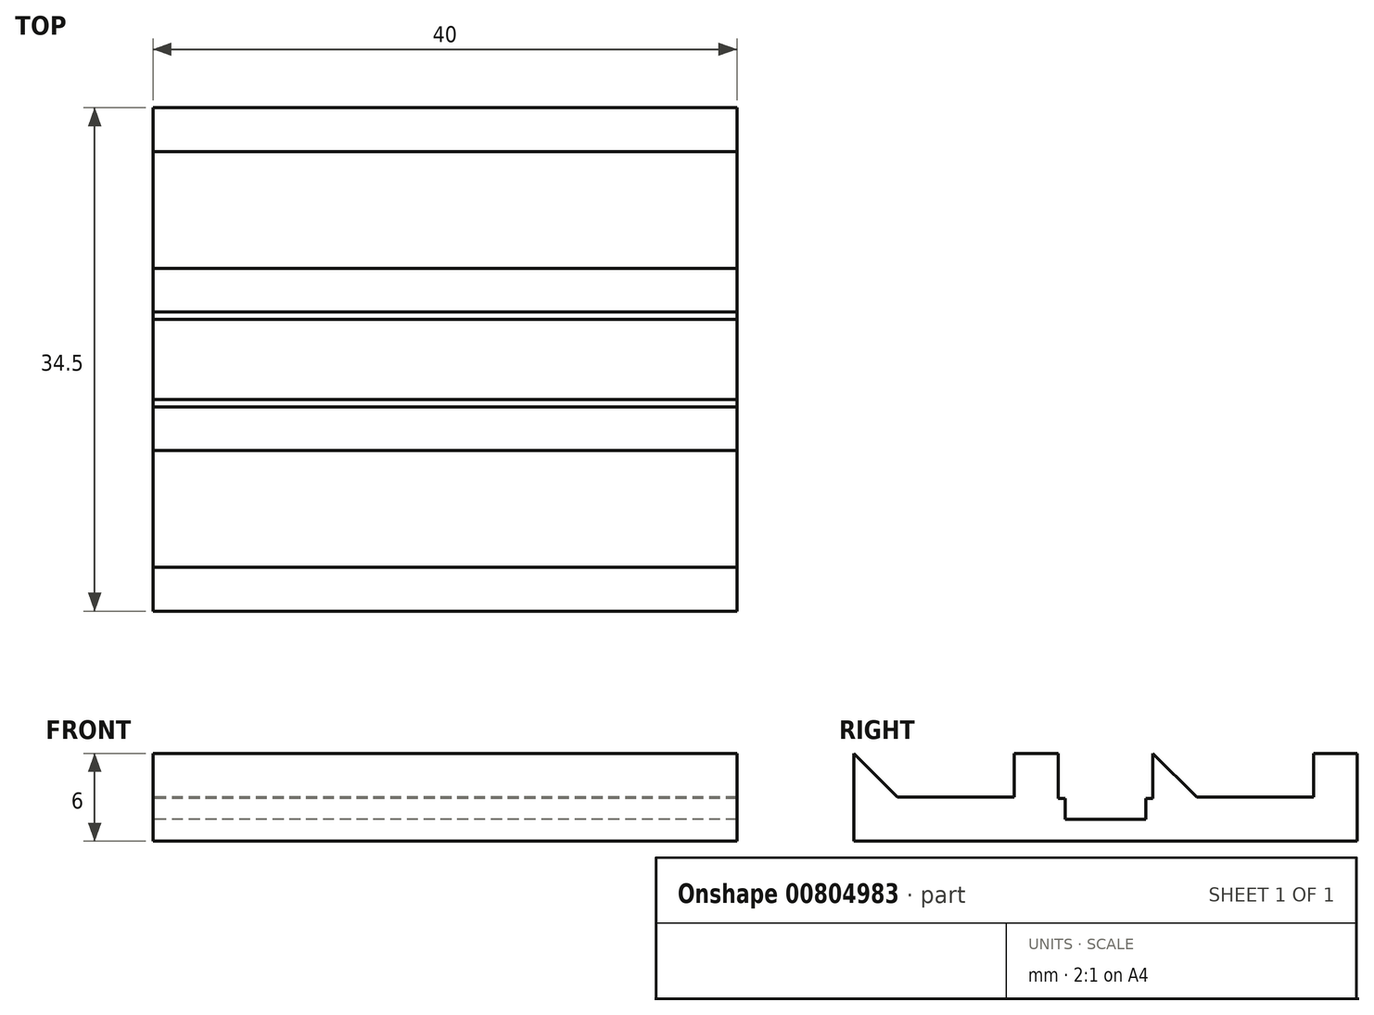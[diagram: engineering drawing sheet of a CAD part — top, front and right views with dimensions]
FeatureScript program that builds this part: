
annotation { "Feature Type Name" : "Feature", "Feature Type Description" : "" }
export const myFeature = defineFeature(function(context is Context, id is Id, definition is map)
    precondition{}
    {
        {
            var Q0;
            Q0=qCreatedBy(makeId("Top.planeOp"),FACE);
            var sketch = newSketch(context, id + "F0", { "sketchPlane" : qUnion([Q0])});
            skLineSegment(sketch, "E0.bottom", {"start": v(0, 0) * mm, "end": v(20, 0) * mm});
            skLineSegment(sketch, "E0.top", {"start": v(0, 34.5) * mm, "end": v(20, 34.5) * mm});
            skLineSegment(sketch, "E0.left", {"start": v(0, 0) * mm, "end": v(0, 34.5) * mm});
            skLineSegment(sketch, "E0.right", {"start": v(20, 0) * mm, "end": v(20, 34.5) * mm});
            skSolve(sketch);
        }
        {
            var Q0;
            Q0=makeQuery(id+"F0.imprint","IMPRINT",FACE,{"disambiguationData":[TD([[makeQuery(id+"F0.imprint","IMPRINT",EDGE,{"derivedFrom":sQuery(id+"F0.wireOp",EDGE,"E0.bottom")}),1.0]])]});
            extrude(context, id + "F1", {"entities" : qUnion([Q0]), "depth" : 6 * mm, "offsetDistance" : 25 * mm});
        }
        {
            var Q0;
            Q0=makeQuery(id+"F1.opExtrude","SWEPT_FACE",FACE,{"disambiguationData":[OSD([sQuery(id+"F0.wireOp",EDGE,"E0.right")])]});
            extrude(context, id + "F2", {"entities" : qUnion([Q0]), "operationType" : NewBodyOperationType.ADD, "depth" : 20 * mm, "offsetDistance" : 25 * mm});
        }
        {
            var Q0;
            Q0=makeQuery(id+"F1.opExtrude","SWEPT_FACE",FACE,{"disambiguationData":[OSD([sQuery(id+"F0.wireOp",EDGE,"E0.left")])]});
            var sketch = newSketch(context, id + "F3", { "sketchPlane" : qUnion([Q0])});
            skLineSegment(sketch, "E1.bottom", {"start": v(-14.5, 6.5) * mm, "end": v(-20, 6.5) * mm});
            skLineSegment(sketch, "E1.top", {"start": v(-14.5, 1.5) * mm, "end": v(-20, 1.5) * mm});
            skLineSegment(sketch, "E1.left", {"start": v(-14.5, 6.5) * mm, "end": v(-14.5, 1.5) * mm});
            skLineSegment(sketch, "E1.right", {"start": v(-20, 6.5) * mm, "end": v(-20, 1.5) * mm});
            skLineSegment(sketch, "E2.bottom", {"start": v(-20.5, 9.04) * mm, "end": v(-14, 9.04) * mm});
            skLineSegment(sketch, "E2.top", {"start": v(-20.5, 2.92) * mm, "end": v(-14, 2.92) * mm});
            skLineSegment(sketch, "E2.left", {"start": v(-20.5, 9.04) * mm, "end": v(-20.5, 2.92) * mm});
            skLineSegment(sketch, "E2.right", {"start": v(-14, 9.04) * mm, "end": v(-14, 2.92) * mm});
            skSolve(sketch);
        }
        {
            var Q0;
            {var subQ2=sQuery(id+"F3.wireOp",EDGE,"E1.bottom");Q0=makeQuery(id+"F3.imprint","IMPRINT",FACE,{"disambiguationData":[TD([[makeQuery(id+"F3.imprint","IMPRINT",EDGE,{"derivedFrom":subQ2}),-1.0]])]});}
            var Q1;
            {var subQ0=sQuery(id+"F3.wireOp",EDGE,"E2.top");var subQ1=sQuery(id+"F3.wireOp",EDGE,"E1.left");var subQ2=makeQuery(id+"F3.imprint","INTERSECT",VERTEX,{"derivedFrom":[subQ1,subQ0]});Q1=makeQuery(id+"F3.imprint","IMPRINT",FACE,{"disambiguationData":[TD([[makeQuery(id+"F3.imprint","IMPRINT",EDGE,{"disambiguationData":[TD([[subQ2,1.0]])],"derivedFrom":subQ1}),-1.0]])]});}
            var Q2;
            {var subQ0=sQuery(id+"F3.wireOp",EDGE,"E2.top");var subQ1=sQuery(id+"F3.wireOp",EDGE,"E1.left");var subQ2=makeQuery(id+"F3.imprint","INTERSECT",VERTEX,{"derivedFrom":[subQ1,subQ0]});Q2=makeQuery(id+"F3.imprint","IMPRINT",FACE,{"disambiguationData":[TD([[makeQuery(id+"F3.imprint","IMPRINT",EDGE,{"disambiguationData":[TD([[subQ2,1.0]])],"derivedFrom":subQ1}),1.0]])]});}
            var Q3;
            {var subQ0=sQuery(id+"F3.wireOp",EDGE,"E2.top");var subQ1=sQuery(id+"F3.wireOp",EDGE,"E1.right");var subQ2=makeQuery(id+"F3.imprint","INTERSECT",VERTEX,{"derivedFrom":[subQ1,subQ0]});Q3=makeQuery(id+"F3.imprint","IMPRINT",FACE,{"disambiguationData":[TD([[makeQuery(id+"F3.imprint","IMPRINT",EDGE,{"disambiguationData":[TD([[subQ2,1.0]])],"derivedFrom":subQ1}),-1.0]])]});}
            var Q4;
            {var subQ0=sQuery(id+"F3.wireOp",EDGE,"E1.top");Q4=makeQuery(id+"F3.imprint","IMPRINT",FACE,{"disambiguationData":[TD([[makeQuery(id+"F3.imprint","IMPRINT",EDGE,{"derivedFrom":subQ0}),-1.0]])]});}
            extrude(context, id + "F4", {"entities" : qUnion([Q0, Q1, Q2, Q3, Q4]), "operationType" : NewBodyOperationType.REMOVE, "oppositeDirection" : true, "depth" : 50 * mm, "offsetDistance" : 25 * mm});
        }
        {
            var Q0;
            Q0=makeQuery(id+"F1.opExtrude","SWEPT_FACE",FACE,{"disambiguationData":[OSD([sQuery(id+"F0.wireOp",EDGE,"E0.left")])]});
            var sketch = newSketch(context, id + "F5", { "sketchPlane" : qUnion([Q0])});
            skLineSegment(sketch, "E3.bottom", {"start": v(-20.5, 6) * mm, "end": v(-21, 6) * mm});
            skLineSegment(sketch, "E3.top", {"start": v(-20.5, 6.5) * mm, "end": v(-21, 6.5) * mm});
            skLineSegment(sketch, "E3.left", {"start": v(-20.5, 6) * mm, "end": v(-20.5, 6.5) * mm});
            skLineSegment(sketch, "E3.right", {"start": v(-21, 6) * mm, "end": v(-21, 6.5) * mm});
            skLineSegment(sketch, "E4.bottom", {"start": v(-14, 6) * mm, "end": v(-13.5, 6) * mm});
            skLineSegment(sketch, "E4.top", {"start": v(-14, 6.5) * mm, "end": v(-13.5, 6.5) * mm});
            skLineSegment(sketch, "E4.left", {"start": v(-14, 6) * mm, "end": v(-14, 6.5) * mm});
            skLineSegment(sketch, "E4.right", {"start": v(-13.5, 6) * mm, "end": v(-13.5, 6.5) * mm});
            skLineSegment(sketch, "E5.bottom", {"start": v(-11, 6) * mm, "end": v(-3, 6) * mm});
            skLineSegment(sketch, "E5.top", {"start": v(-11, 3) * mm, "end": v(-3, 3) * mm});
            skLineSegment(sketch, "E5.left", {"start": v(-11, 6) * mm, "end": v(-11, 3) * mm});
            skLineSegment(sketch, "E5.right", {"start": v(-3, 6) * mm, "end": v(-3, 3) * mm});
            skLineSegment(sketch, "E6.bottom", {"start": v(-23.5, 6) * mm, "end": v(-31.5, 6) * mm});
            skLineSegment(sketch, "E6.top", {"start": v(-23.5, 3) * mm, "end": v(-31.5, 3) * mm});
            skLineSegment(sketch, "E6.left", {"start": v(-23.5, 6) * mm, "end": v(-23.5, 3) * mm});
            skLineSegment(sketch, "E6.right", {"start": v(-31.5, 6) * mm, "end": v(-31.5, 3) * mm});
            skSolve(sketch);
        }
        {
            var Q0;
            Q0=makeQuery(id+"F5.imprint","IMPRINT",FACE,{"disambiguationData":[TD([[makeQuery(id+"F5.imprint","IMPRINT",EDGE,{"derivedFrom":sQuery(id+"F5.wireOp",EDGE,"E6.bottom")}),1.0]])]});
            var Q1;
            Q1=makeQuery(id+"F5.imprint","IMPRINT",FACE,{"disambiguationData":[TD([[makeQuery(id+"F5.imprint","IMPRINT",EDGE,{"derivedFrom":sQuery(id+"F5.wireOp",EDGE,"E5.bottom")}),1.0]])]});
            extrude(context, id + "F6", {"entities" : qUnion([Q0, Q1]), "operationType" : NewBodyOperationType.REMOVE, "oppositeDirection" : true, "depth" : 50 * mm, "offsetDistance" : 25 * mm});
        }
        {
            var Q0;
            Q0=makeQuery(id+"F6.boolean.opBoolean","COPY",EDGE,{"derivedFrom":makeQuery(id+"F6.opExtrude","SWEPT_EDGE",EDGE,{"disambiguationData":[OSD([sQuery(id+"F0.wireOp",EDGE,"E0.left"),sQuery(id+"F5.wireOp",EDGE,"E5.bottom"),sQuery(id+"F5.wireOp",EDGE,"E5.left")])]})});
            var Q1;
            Q1=makeQuery(id+"F6.boolean.opBoolean","COPY",EDGE,{"derivedFrom":makeQuery(id+"F6.opExtrude","SWEPT_EDGE",EDGE,{"disambiguationData":[OSD([sQuery(id+"F0.wireOp",EDGE,"E0.left"),sQuery(id+"F5.wireOp",EDGE,"E5.bottom"),sQuery(id+"F5.wireOp",EDGE,"E5.right")])]})});
            var Q2;
            Q2=makeQuery(id+"F6.boolean.opBoolean","COPY",EDGE,{"derivedFrom":makeQuery(id+"F6.opExtrude","SWEPT_EDGE",EDGE,{"disambiguationData":[OSD([sQuery(id+"F0.wireOp",EDGE,"E0.left"),sQuery(id+"F5.wireOp",EDGE,"E6.bottom"),sQuery(id+"F5.wireOp",EDGE,"E6.right")])]})});
            var Q3;
            Q3=makeQuery(id+"F6.boolean.opBoolean","COPY",EDGE,{"derivedFrom":makeQuery(id+"F6.opExtrude","SWEPT_EDGE",EDGE,{"disambiguationData":[OSD([sQuery(id+"F0.wireOp",EDGE,"E0.left"),sQuery(id+"F5.wireOp",EDGE,"E6.bottom"),sQuery(id+"F5.wireOp",EDGE,"E6.left")])]})});
            chamfer(context, id + "F7", {"entities" : qUnion([Q0, Q1, Q2, Q3]), "width" : 3 * mm, "tangentPropagation" : true});
        }
    });
